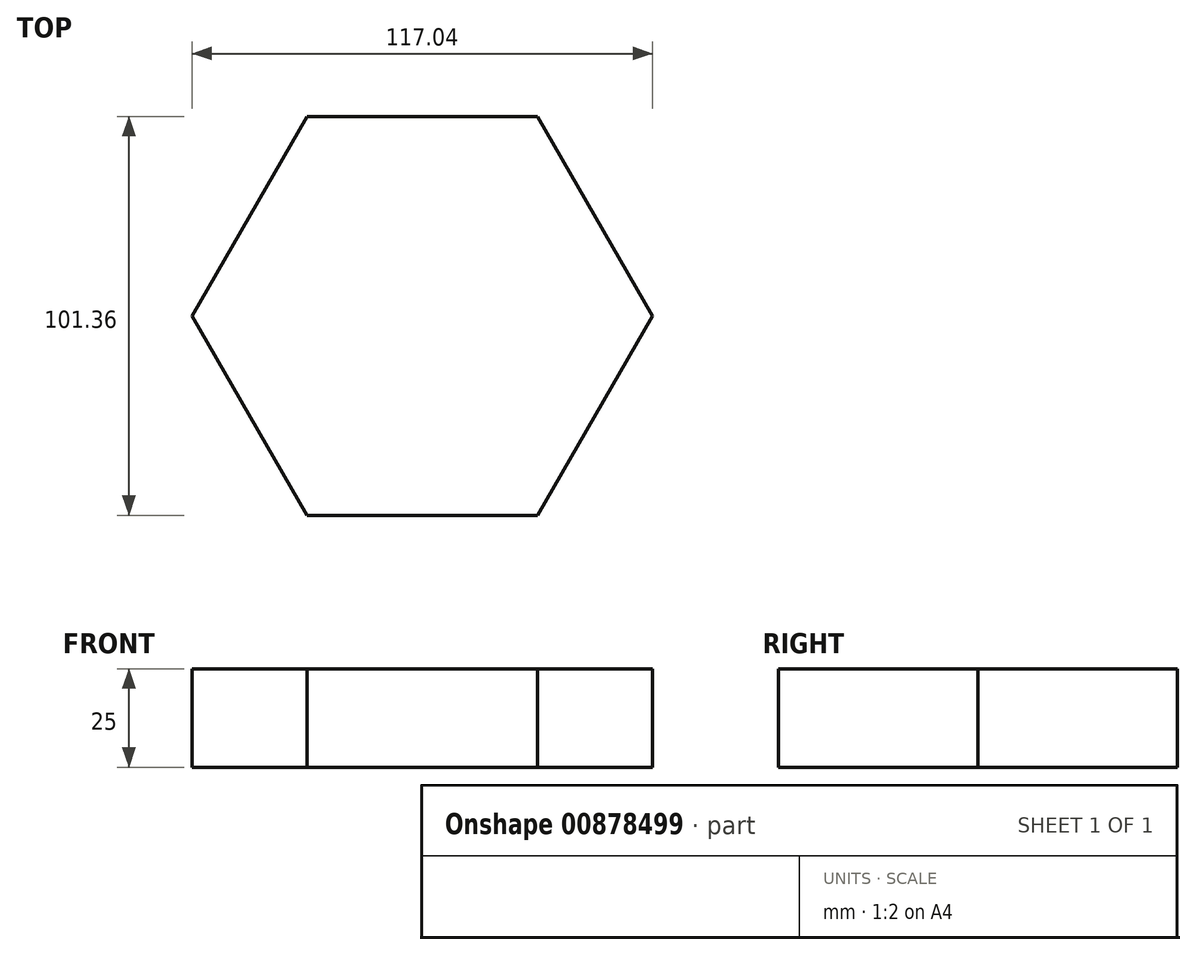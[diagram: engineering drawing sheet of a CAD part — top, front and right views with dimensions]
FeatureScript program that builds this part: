
annotation { "Feature Type Name" : "Feature", "Feature Type Description" : "" }
export const myFeature = defineFeature(function(context is Context, id is Id, definition is map)
    precondition{}
    {
        {
            var Q0;
            Q0=qCreatedBy(makeId("Top.planeOp"),FACE);
            var sketch = newSketch(context, id + "F0", { "sketchPlane" : qUnion([Q0])});
            skCircle(sketch, "E0.cCircle", {"center": v(0, 0) * mm, "radius": 50.68 * mm, "construction": true});
            skLineSegment(sketch, "E0.0", {"start": v(-29.26, 50.68) * mm, "end": v(29.26, 50.68) * mm});
            skLineSegment(sketch, "E0.1", {"start": v(29.26, 50.68) * mm, "end": v(58.52, 0) * mm});
            skLineSegment(sketch, "E0.2", {"start": v(58.52, 0) * mm, "end": v(29.26, -50.68) * mm});
            skLineSegment(sketch, "E0.3", {"start": v(29.26, -50.68) * mm, "end": v(-29.26, -50.68) * mm});
            skLineSegment(sketch, "E0.4", {"start": v(-29.26, -50.68) * mm, "end": v(-58.52, 0) * mm});
            skLineSegment(sketch, "E0.5", {"start": v(-58.52, 0) * mm, "end": v(-29.26, 50.68) * mm});
            skPoint(sketch, "E0.0.midPoint", {"position": v(0, 50.68) * mm});
            skSolve(sketch);
        }
        {
            var Q0;
            Q0=makeQuery(id+"F0.imprint","IMPRINT",FACE,{"disambiguationData":[TD([[makeQuery(id+"F0.imprint","IMPRINT",EDGE,{"derivedFrom":sQuery(id+"F0.wireOp",EDGE,"E0.0")}),-1.0]])]});
            extrude(context, id + "F1", {"entities" : qUnion([Q0]), "depth" : 25 * mm, "offsetDistance" : 25 * mm});
        }
    });
